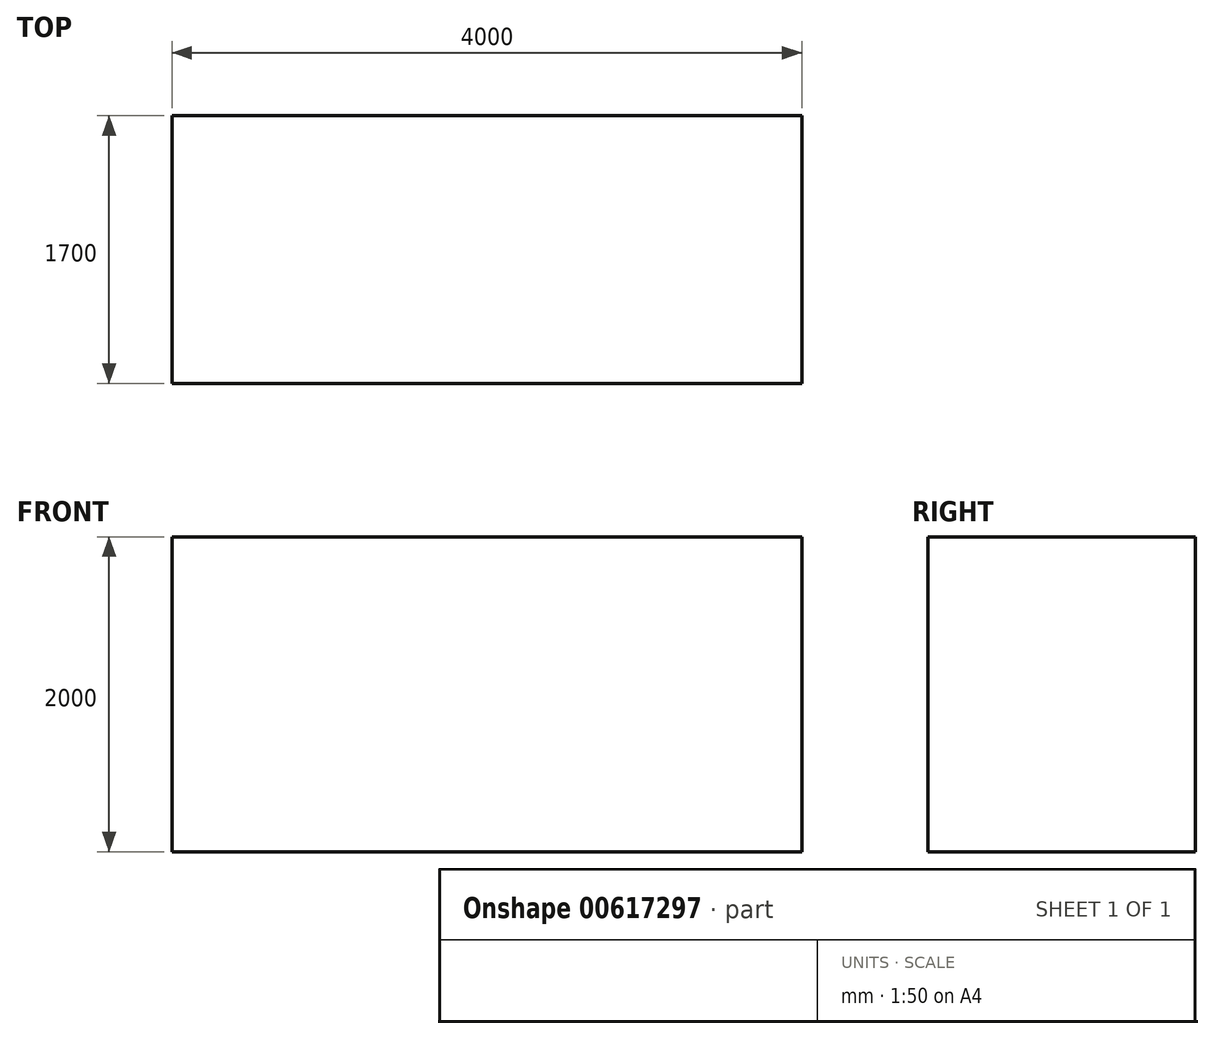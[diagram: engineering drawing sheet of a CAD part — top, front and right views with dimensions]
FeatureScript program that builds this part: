
annotation { "Feature Type Name" : "Feature", "Feature Type Description" : "" }
export const myFeature = defineFeature(function(context is Context, id is Id, definition is map)
    precondition{}
    {
        {
            var Q0;
            Q0=qCreatedBy(makeId("Top.planeOp"),FACE);
            var sketch = newSketch(context, id + "F0", { "sketchPlane" : qUnion([Q0])});
            skLineSegment(sketch, "E0.bottom", {"start": v(-1998.84, 245.57) * mm, "end": v(2001.16, 245.57) * mm});
            skLineSegment(sketch, "E0.top", {"start": v(-1998.84, -1454.43) * mm, "end": v(2001.16, -1454.43) * mm});
            skLineSegment(sketch, "E0.left", {"start": v(-1998.84, 245.57) * mm, "end": v(-1998.84, -1454.43) * mm});
            skLineSegment(sketch, "E0.right", {"start": v(2001.16, 245.57) * mm, "end": v(2001.16, -1454.43) * mm});
            skSolve(sketch);
        }
        {
            var Q0;
            Q0 = qSketchRegion(id + "F0", true);
            extrude(context, id + "F1", {"entities" : qUnion([Q0]), "depth" : 2000 * mm, "offsetDistance" : 25 * mm});
        }
    });
